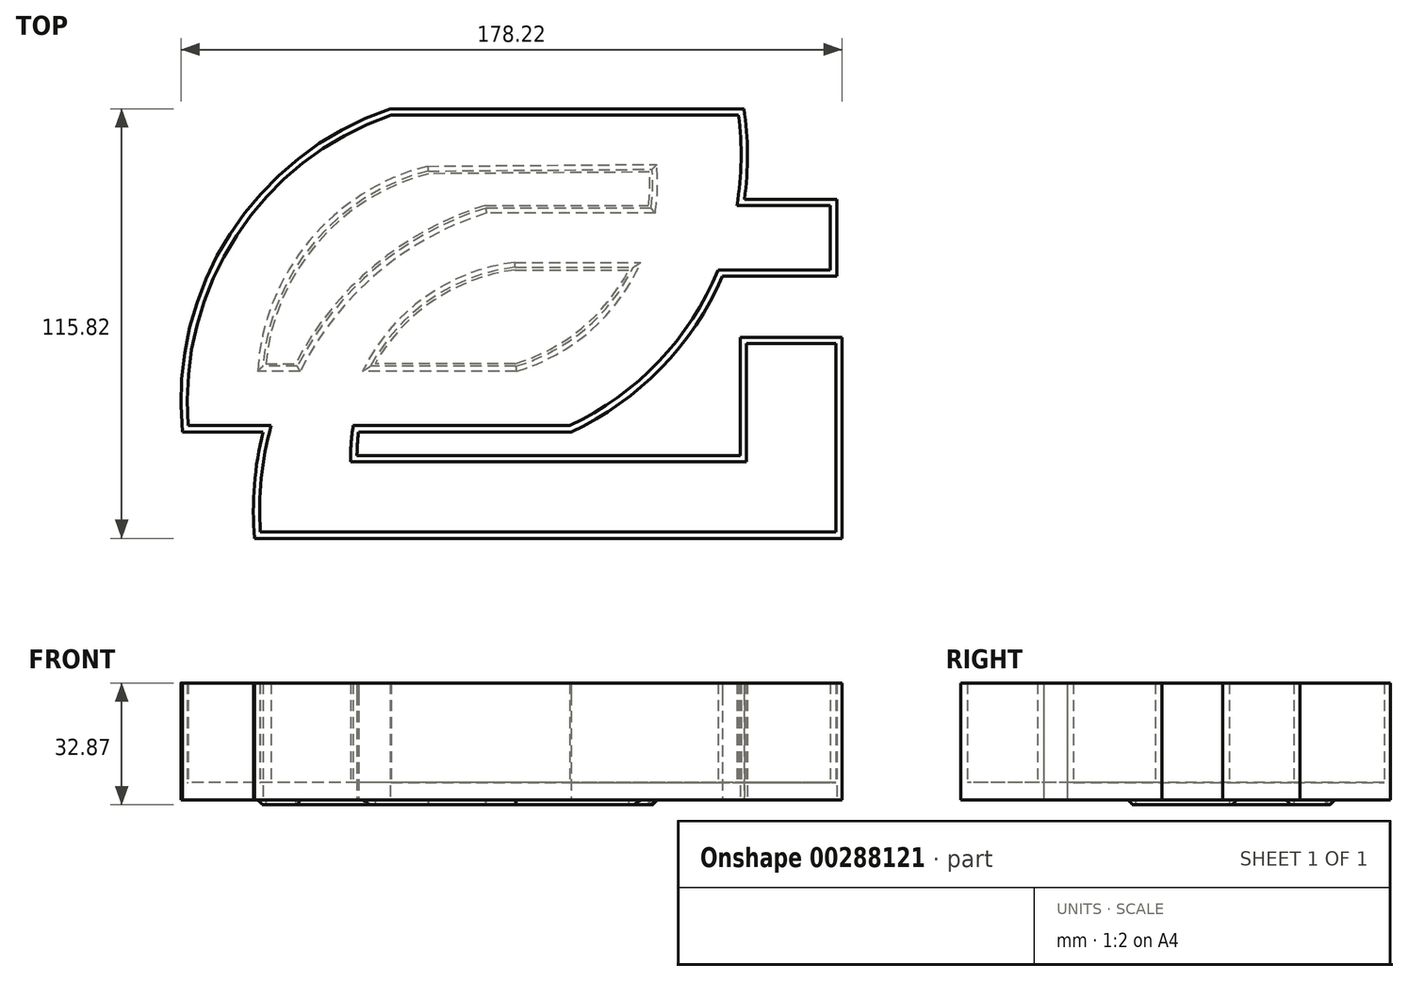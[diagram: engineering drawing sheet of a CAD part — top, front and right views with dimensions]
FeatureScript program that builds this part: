
annotation { "Feature Type Name" : "Feature", "Feature Type Description" : "" }
export const myFeature = defineFeature(function(context is Context, id is Id, definition is map)
    precondition{}
    {
        {
            assignVariable(context, id + "F0", {"name" : "wt", "anyValue" : 1.7});
        }
        {
            assignVariable(context, id + "F1", {"name" : "wd", "anyValue" : 28.57 * mm});
        }
        {
            var Q0;
            Q0=qCreatedBy(makeId("Top.planeOp"),FACE);
            var sketch = newSketch(context, id + "F2", { "sketchPlane" : qUnion([Q0])});
            skLineSegment(sketch, "E0", {"start": v(61.61, -3.74) * mm, "end": v(89.1, -3.74) * mm});
            skLineSegment(sketch, "E1", {"start": v(89.1, -3.74) * mm, "end": v(89.1, -57.9) * mm});
            skLineSegment(sketch, "E2", {"start": v(89.1, -57.9) * mm, "end": v(-69.28, -57.9) * mm});
            skLineSegment(sketch, "E3", {"start": v(61.61, -3.74) * mm, "end": v(61.61, -35.58) * mm});
            skLineSegment(sketch, "E4", {"start": v(61.61, -35.58) * mm, "end": v(-41.66, -35.58) * mm});
            skArc(sketch, "E5", {"start": v(1.12, 12.73) * mm, "mid": v(-29.38, -3.36) * mm, "end": v(-41.66, -35.58) * mm});
            skLineSegment(sketch, "E6", {"start": v(1.12, 12.73) * mm, "end": v(28.71, 12.73) * mm});
            skLineSegment(sketch, "E7", {"start": v(56.87, 12.73) * mm, "end": v(87.68, 12.73) * mm});
            skLineSegment(sketch, "E8", {"start": v(87.68, 12.73) * mm, "end": v(87.68, 33.53) * mm});
            skLineSegment(sketch, "E9", {"start": v(87.68, 33.53) * mm, "end": v(61.61, 33.53) * mm});
            skLineSegment(sketch, "E10", {"start": v(35.42, 33.53) * mm, "end": v(-7.33, 33.53) * mm});
            skArc(sketch, "E11", {"start": v(-7.33, 33.53) * mm, "mid": v(-54.5, -1.23) * mm, "end": v(-69.28, -57.9) * mm});
            skArc(sketch, "E12", {"start": v(-32.72, 57.9) * mm, "mid": v(-75.9, 24.1) * mm, "end": v(-88.7, -29.22) * mm});
            skLineSegment(sketch, "E13", {"start": v(-32.72, 57.9) * mm, "end": v(62.63, 57.9) * mm});
            skArc(sketch, "E14", {"start": v(16.1, -29.22) * mm, "mid": v(53.9, 6.58) * mm, "end": v(62.63, 57.9) * mm});
            skLineSegment(sketch, "E15", {"start": v(16.1, -29.22) * mm, "end": v(-41.22, -29.22) * mm});
            skLineSegment(sketch, "E16", {"start": v(-67, -29.22) * mm, "end": v(-88.7, -29.22) * mm});
            skArc(sketch, "E17", {"start": v(-22.14, 38.67) * mm, "mid": v(-50.54, 21.24) * mm, "end": v(-64.34, -9.1) * mm});
            skLineSegment(sketch, "E18", {"start": v(-22.14, 38.67) * mm, "end": v(35.58, 39.1) * mm});
            skArc(sketch, "E19", {"start": v(0.76, -9.1) * mm, "mid": v(26.34, 9.11) * mm, "end": v(35.58, 39.1) * mm});
            skLineSegment(sketch, "E20", {"start": v(0.76, -9.1) * mm, "end": v(-33.75, -9.1) * mm});
            skLineSegment(sketch, "E21", {"start": v(-59.24, -9.1) * mm, "end": v(-64.34, -9.1) * mm});
            skSolve(sketch);
        }
        {
            var Q0;
            Q0=makeQuery(id+"F2.imprint","IMPRINT",FACE,{"disambiguationData":[TD([[makeQuery(id+"F2.imprint","IMPRINT",EDGE,{"derivedFrom":sQuery(id+"F2.wireOp",EDGE,"E12")}),1.0]])]});
            extrude(context, id + "F3", {"entities" : qUnion([Q0]), "depth" : getVariable(context, 'wd')});
        }
        {
            var Q0;
            Q0=makeQuery(id+"F2.imprint","IMPRINT",FACE,{"disambiguationData":[TD([[makeQuery(id+"F2.imprint","IMPRINT",EDGE,{"derivedFrom":sQuery(id+"F2.wireOp",EDGE,"E0")}),-1.0]])]});
            extrude(context, id + "F4", {"entities" : qUnion([Q0]), "operationType" : NewBodyOperationType.ADD, "depth" : getVariable(context, 'wd')});
        }
        {
            var Q0;
            {var subQ0=sQuery(id+"F2.wireOp",EDGE,"E7");Q0=makeQuery(id+"F2.imprint","IMPRINT",FACE,{"disambiguationData":[TD([[makeQuery(id+"F2.imprint","IMPRINT",EDGE,{"derivedFrom":subQ0}),1.0]])]});}
            extrude(context, id + "F5", {"entities" : qUnion([Q0]), "operationType" : NewBodyOperationType.ADD, "depth" : getVariable(context, 'wd')});
        }
        {
            var Q0;
            Q0=makeQuery(id+"F3.opExtrude","CAP_FACE",FACE,{"disambiguationData":[OSD([sQuery(id+"F2.wireOp",EDGE,"E5"),sQuery(id+"F2.wireOp",EDGE,"E11"),sQuery(id+"F2.wireOp",EDGE,"E12"),sQuery(id+"F2.wireOp",EDGE,"E13"),sQuery(id+"F2.wireOp",EDGE,"E14"),sQuery(id+"F2.wireOp",EDGE,"E15"),sQuery(id+"F2.wireOp",EDGE,"E16"),sQuery(id+"F2.wireOp",EDGE,"E17"),sQuery(id+"F2.wireOp",EDGE,"E18"),sQuery(id+"F2.wireOp",EDGE,"E19"),sQuery(id+"F2.wireOp",EDGE,"E20"),sQuery(id+"F2.wireOp",EDGE,"E21")])],"isStart":false});
            var Q1;
            Q1=makeQuery(id+"F4.opExtrude","CAP_FACE",FACE,{"disambiguationData":[OSD([sQuery(id+"F2.wireOp",EDGE,"E0"),sQuery(id+"F2.wireOp",EDGE,"E1"),sQuery(id+"F2.wireOp",EDGE,"E2"),sQuery(id+"F2.wireOp",EDGE,"E3"),sQuery(id+"F2.wireOp",EDGE,"E4"),sQuery(id+"F2.wireOp",EDGE,"E5"),sQuery(id+"F2.wireOp",EDGE,"E6"),sQuery(id+"F2.wireOp",EDGE,"E10"),sQuery(id+"F2.wireOp",EDGE,"E11"),sQuery(id+"F2.wireOp",EDGE,"E19")])],"isStart":false});
            var Q2;
            Q2=makeQuery(id+"F5.opExtrude","CAP_FACE",FACE,{"disambiguationData":[OSD([sQuery(id+"F2.wireOp",EDGE,"E7"),sQuery(id+"F2.wireOp",EDGE,"E8"),sQuery(id+"F2.wireOp",EDGE,"E9"),sQuery(id+"F2.wireOp",EDGE,"E14")])],"isStart":false});
            shell(context, id + "F6", {"entities" : qUnion([Q0, Q1, Q2]), "thickness" : (getVariable(context, 'wt')) * mm});
        }
        {
            var Q0;
            {var subQ0=sQuery(id+"F2.wireOp",EDGE,"E14");var subQ1=sQuery(id+"F2.wireOp",EDGE,"E9");var subQ2=sQuery(id+"F2.wireOp",EDGE,"E8");var subQ3=sQuery(id+"F2.wireOp",EDGE,"E7");var subQ4=sQuery(id+"F2.wireOp",EDGE,"E19");var subQ5=sQuery(id+"F2.wireOp",EDGE,"E11");var subQ6=sQuery(id+"F2.wireOp",EDGE,"E10");var subQ7=sQuery(id+"F2.wireOp",EDGE,"E6");var subQ8=sQuery(id+"F2.wireOp",EDGE,"E5");var subQ9=sQuery(id+"F2.wireOp",EDGE,"E4");var subQ10=sQuery(id+"F2.wireOp",EDGE,"E3");var subQ11=sQuery(id+"F2.wireOp",EDGE,"E2");var subQ12=sQuery(id+"F2.wireOp",EDGE,"E1");var subQ13=sQuery(id+"F2.wireOp",EDGE,"E0");var subQ14=sQuery(id+"F2.wireOp",EDGE,"E21");var subQ15=sQuery(id+"F2.wireOp",EDGE,"E20");var subQ16=sQuery(id+"F2.wireOp",EDGE,"E18");var subQ17=sQuery(id+"F2.wireOp",EDGE,"E17");var subQ18=sQuery(id+"F2.wireOp",EDGE,"E16");var subQ19=sQuery(id+"F2.wireOp",EDGE,"E15");var subQ20=sQuery(id+"F2.wireOp",EDGE,"E13");var subQ21=sQuery(id+"F2.wireOp",EDGE,"E12");Q0=makeQuery(id+"F6.opShell","OFFSET_FACE",FACE,{"disambiguationData":[OSD([subQ13,subQ12,subQ11,subQ10,subQ9,subQ8,subQ7,subQ3,subQ2,subQ1,subQ6,subQ5,subQ21,subQ20,subQ0,subQ19,subQ18,subQ17,subQ16,subQ4,subQ15,subQ14]),TDD([makeQuery(id+"F5.boolean.opBoolean","MERGE",FACE,{"derivedFrom":[makeQuery(id+"F4.boolean.opBoolean","MERGE",FACE,{"derivedFrom":[makeQuery(id+"F3.opExtrude","CAP_FACE",FACE,{"disambiguationData":[OSD([subQ8,subQ5,subQ21,subQ20,subQ0,subQ19,subQ18,subQ17,subQ16,subQ4,subQ15,subQ14])],"isStart":false}),makeQuery(id+"F4.opExtrude","CAP_FACE",FACE,{"disambiguationData":[OSD([subQ13,subQ12,subQ11,subQ10,subQ9,subQ8,subQ7,subQ6,subQ5,subQ4])],"isStart":false})]}),makeQuery(id+"F5.opExtrude","CAP_FACE",FACE,{"disambiguationData":[OSD([subQ3,subQ2,subQ1,subQ0])],"isStart":false})]})]),OD(0.0)]});}
            cPlane(context, id + "F7", {"entities" : qUnion([Q0]), "cplaneType" : CPlaneType.OFFSET, "offset" : 3 * mm, "oppositeDirection" : true, "width" : 150 * mm, "height" : 150 * mm});
        }
        {
            var Q0;
            Q0=qCreatedBy(id+"F7.planeOp",FACE);
            var sketch = newSketch(context, id + "F8", { "sketchPlane" : qUnion([Q0])});
            skArc(sketch, "E22.0.0", {"start": v(-41.66, -35.58) * mm, "mid": v(-41.54, -32.4) * mm, "end": v(-41.22, -29.22) * mm});
            skLineSegment(sketch, "E22.0.1", {"start": v(-41.22, -29.22) * mm, "end": v(16.1, -29.22) * mm});
            skArc(sketch, "E22.0.2", {"start": v(16.1, -29.22) * mm, "mid": v(40.34, -12) * mm, "end": v(56.87, 12.73) * mm});
            skLineSegment(sketch, "E22.0.3", {"start": v(56.87, 12.73) * mm, "end": v(87.68, 12.73) * mm});
            skLineSegment(sketch, "E22.0.4", {"start": v(87.68, 12.73) * mm, "end": v(87.68, 33.53) * mm});
            skLineSegment(sketch, "E22.0.5", {"start": v(87.68, 33.53) * mm, "end": v(62.75, 33.53) * mm});
            skArc(sketch, "E22.0.6", {"start": v(62.75, 33.53) * mm, "mid": v(63.6, 45.72) * mm, "end": v(62.63, 57.9) * mm});
            skLineSegment(sketch, "E22.0.7", {"start": v(62.63, 57.9) * mm, "end": v(-32.72, 57.9) * mm});
            skArc(sketch, "E22.0.8", {"start": v(-32.72, 57.9) * mm, "mid": v(-75.9, 24.1) * mm, "end": v(-88.7, -29.22) * mm});
            skLineSegment(sketch, "E22.0.9", {"start": v(-88.7, -29.22) * mm, "end": v(-67, -29.22) * mm});
            skArc(sketch, "E22.0.10", {"start": v(-67, -29.22) * mm, "mid": v(-69.32, -43.47) * mm, "end": v(-69.28, -57.9) * mm});
            skLineSegment(sketch, "E22.0.11", {"start": v(-69.28, -57.9) * mm, "end": v(89.1, -57.9) * mm});
            skLineSegment(sketch, "E22.0.12", {"start": v(89.1, -57.9) * mm, "end": v(89.1, -3.74) * mm});
            skLineSegment(sketch, "E22.0.13", {"start": v(89.1, -3.74) * mm, "end": v(61.61, -3.74) * mm});
            skLineSegment(sketch, "E22.0.14", {"start": v(61.61, -3.74) * mm, "end": v(61.61, -35.58) * mm});
            skLineSegment(sketch, "E22.0.15", {"start": v(61.61, -35.58) * mm, "end": v(-41.66, -35.58) * mm});
            skLineSegment(sketch, "E23.0.0", {"start": v(-36.77, -10.8) * mm, "end": v(1.01, -10.8) * mm});
            skArc(sketch, "E23.0.1", {"start": v(1.01, -10.8) * mm, "mid": v(18.88, -1.3) * mm, "end": v(31.6, 14.43) * mm});
            skLineSegment(sketch, "E23.0.2", {"start": v(31.6, 14.43) * mm, "end": v(1.01, 14.43) * mm});
            skArc(sketch, "E23.0.3", {"start": v(1.01, 14.43) * mm, "mid": v(-20.87, 6.3) * mm, "end": v(-36.77, -10.8) * mm});
            skLineSegment(sketch, "E24.0.0", {"start": v(-7.08, 31.83) * mm, "end": v(36.95, 31.83) * mm});
            skArc(sketch, "E24.0.1", {"start": v(36.95, 31.83) * mm, "mid": v(37.28, 36.32) * mm, "end": v(37.2, 40.82) * mm});
            skLineSegment(sketch, "E24.0.2", {"start": v(37.2, 40.82) * mm, "end": v(-22.37, 40.37) * mm});
            skArc(sketch, "E24.0.3", {"start": v(-22.37, 40.37) * mm, "mid": v(-52.38, 21.71) * mm, "end": v(-66.24, -10.8) * mm});
            skLineSegment(sketch, "E24.0.4", {"start": v(-66.24, -10.8) * mm, "end": v(-58.22, -10.8) * mm});
            skArc(sketch, "E24.0.5", {"start": v(-58.22, -10.8) * mm, "mid": v(-36.94, 15.66) * mm, "end": v(-7.08, 31.83) * mm});
            skArc(sketch, "E25.0", {"start": v(-32.43, 56.2) * mm, "mid": v(-74.13, 23.72) * mm, "end": v(-87.14, -27.52) * mm});
            skLineSegment(sketch, "E26.0.0", {"start": v(-64.79, -27.52) * mm, "end": v(-87.14, -27.52) * mm});
            skLineSegment(sketch, "E26.0.2", {"start": v(-87.14, -27.52) * mm, "end": v(-64.79, -27.52) * mm});
            skArc(sketch, "E27.0.0", {"start": v(-64.79, -27.52) * mm, "mid": v(-67.46, -41.74) * mm, "end": v(-67.7, -56.2) * mm});
            skArc(sketch, "E27.0.2", {"start": v(-67.7, -56.2) * mm, "mid": v(-67.46, -41.74) * mm, "end": v(-64.79, -27.52) * mm});
            skLineSegment(sketch, "E28.0.0", {"start": v(-32.43, 56.2) * mm, "end": v(61.16, 56.2) * mm});
            skLineSegment(sketch, "E28.0.2", {"start": v(61.16, 56.2) * mm, "end": v(-32.43, 56.2) * mm});
            skLineSegment(sketch, "E29.0.0", {"start": v(87.4, -56.2) * mm, "end": v(-67.7, -56.2) * mm});
            skLineSegment(sketch, "E29.0.2", {"start": v(-67.7, -56.2) * mm, "end": v(87.4, -56.2) * mm});
            skLineSegment(sketch, "E30.0.0", {"start": v(-43.34, -37.28) * mm, "end": v(63.31, -37.28) * mm});
            skLineSegment(sketch, "E30.0.2", {"start": v(63.31, -37.28) * mm, "end": v(-43.34, -37.28) * mm});
            skLineSegment(sketch, "E31.0.0", {"start": v(63.31, -5.44) * mm, "end": v(87.4, -5.44) * mm});
            skLineSegment(sketch, "E31.0.2", {"start": v(87.4, -5.44) * mm, "end": v(63.31, -5.44) * mm});
            skLineSegment(sketch, "E32.0.0", {"start": v(87.4, -5.44) * mm, "end": v(87.4, -56.2) * mm});
            skLineSegment(sketch, "E32.0.2", {"start": v(87.4, -56.2) * mm, "end": v(87.4, -5.44) * mm});
            skLineSegment(sketch, "E33.0.0", {"start": v(63.31, -37.28) * mm, "end": v(63.31, -5.44) * mm});
            skLineSegment(sketch, "E33.0.2", {"start": v(63.31, -5.44) * mm, "end": v(63.31, -37.28) * mm});
            skArc(sketch, "E34.0.1", {"start": v(-42.69, -27.52) * mm, "mid": v(-43.25, -32.39) * mm, "end": v(-43.34, -37.28) * mm});
            skArc(sketch, "E34.0.3", {"start": v(-43.34, -37.28) * mm, "mid": v(-43.25, -32.39) * mm, "end": v(-42.69, -27.52) * mm});
            skLineSegment(sketch, "E35.0.0", {"start": v(15.72, -27.52) * mm, "end": v(-42.69, -27.52) * mm});
            skLineSegment(sketch, "E35.0.2", {"start": v(-42.69, -27.52) * mm, "end": v(15.72, -27.52) * mm});
            skArc(sketch, "E36.0.1", {"start": v(55.74, 14.43) * mm, "mid": v(39.64, -10.27) * mm, "end": v(15.72, -27.52) * mm});
            skArc(sketch, "E36.0.3", {"start": v(15.72, -27.52) * mm, "mid": v(39.64, -10.27) * mm, "end": v(55.74, 14.43) * mm});
            skLineSegment(sketch, "E37.0.0", {"start": v(85.98, 14.43) * mm, "end": v(55.74, 14.43) * mm});
            skLineSegment(sketch, "E37.0.2", {"start": v(55.74, 14.43) * mm, "end": v(85.98, 14.43) * mm});
            skLineSegment(sketch, "E38.0.0", {"start": v(85.98, 31.83) * mm, "end": v(85.98, 14.43) * mm});
            skLineSegment(sketch, "E38.0.2", {"start": v(85.98, 14.43) * mm, "end": v(85.98, 31.83) * mm});
            skArc(sketch, "E39.0.0", {"start": v(60.76, 31.83) * mm, "mid": v(61.89, 44) * mm, "end": v(61.16, 56.2) * mm});
            skArc(sketch, "E39.0.2", {"start": v(61.16, 56.2) * mm, "mid": v(61.89, 44) * mm, "end": v(60.76, 31.83) * mm});
            skLineSegment(sketch, "E40.0.0", {"start": v(60.76, 31.83) * mm, "end": v(85.98, 31.83) * mm});
            skLineSegment(sketch, "E40.0.2", {"start": v(85.98, 31.83) * mm, "end": v(60.76, 31.83) * mm});
            skArc(sketch, "E41.0.0", {"start": v(-87.14, -27.52) * mm, "mid": v(-74.13, 23.72) * mm, "end": v(-32.43, 56.2) * mm});
            skArc(sketch, "E42.0", {"start": v(-63.88, -52.2) * mm, "mid": v(-62.9, -37.67) * mm, "end": v(-59.36, -23.52) * mm});
            skLineSegment(sketch, "E42.1", {"start": v(-83.36, -23.52) * mm, "end": v(-59.36, -23.52) * mm});
            skArc(sketch, "E42.2", {"start": v(-31.76, 52.2) * mm, "mid": v(-69.95, 22.78) * mm, "end": v(-83.36, -23.52) * mm});
            skLineSegment(sketch, "E42.3", {"start": v(-31.76, 52.2) * mm, "end": v(57.59, 52.2) * mm});
            skArc(sketch, "E42.4", {"start": v(57.59, 52.2) * mm, "mid": v(57.71, 39.95) * mm, "end": v(55.87, 27.83) * mm});
            skLineSegment(sketch, "E42.5", {"start": v(67.31, -41.28) * mm, "end": v(-47.08, -41.28) * mm});
            skLineSegment(sketch, "E42.6", {"start": v(67.31, -9.44) * mm, "end": v(67.31, -41.28) * mm});
            skLineSegment(sketch, "E42.7", {"start": v(83.4, -9.44) * mm, "end": v(67.31, -9.44) * mm});
            skLineSegment(sketch, "E42.8", {"start": v(83.4, -52.2) * mm, "end": v(83.4, -9.44) * mm});
            skArc(sketch, "E42.9", {"start": v(-47.08, -41.28) * mm, "mid": v(-47.25, -32.36) * mm, "end": v(-45.97, -23.52) * mm});
            skLineSegment(sketch, "E42.10", {"start": v(-45.97, -23.52) * mm, "end": v(14.8, -23.52) * mm});
            skArc(sketch, "E42.11", {"start": v(53.02, 18.43) * mm, "mid": v(37.95, -6.22) * mm, "end": v(14.8, -23.52) * mm});
            skLineSegment(sketch, "E42.12", {"start": v(53.02, 18.43) * mm, "end": v(81.98, 18.43) * mm});
            skLineSegment(sketch, "E42.13", {"start": v(81.98, 18.43) * mm, "end": v(81.98, 27.83) * mm});
            skLineSegment(sketch, "E42.14", {"start": v(-63.88, -52.2) * mm, "end": v(83.4, -52.2) * mm});
            skLineSegment(sketch, "E42.15", {"start": v(81.98, 27.83) * mm, "end": v(55.87, 27.83) * mm});
            skLineSegment(sketch, "E43.0", {"start": v(37.77, 18.43) * mm, "end": v(0.77, 18.43) * mm});
            skArc(sketch, "E43.1", {"start": v(1.58, -14.8) * mm, "mid": v(23.62, -2.48) * mm, "end": v(37.77, 18.43) * mm});
            skLineSegment(sketch, "E43.2", {"start": v(-43.18, -14.8) * mm, "end": v(1.58, -14.8) * mm});
            skArc(sketch, "E43.3", {"start": v(0.77, 18.43) * mm, "mid": v(-25.7, 7.77) * mm, "end": v(-43.18, -14.8) * mm});
            skArc(sketch, "E44.0", {"start": v(-55.75, -14.8) * mm, "mid": v(-35.52, 11.62) * mm, "end": v(-6.47, 27.83) * mm});
            skArc(sketch, "E44.1", {"start": v(40.39, 27.83) * mm, "mid": v(41.28, 36.32) * mm, "end": v(40.84, 44.85) * mm});
            skLineSegment(sketch, "E44.2", {"start": v(40.84, 44.85) * mm, "end": v(-22.88, 44.37) * mm});
            skLineSegment(sketch, "E44.3", {"start": v(-6.47, 27.83) * mm, "end": v(40.39, 27.83) * mm});
            skArc(sketch, "E44.4", {"start": v(-22.88, 44.37) * mm, "mid": v(-56.66, 22.81) * mm, "end": v(-70.5, -14.8) * mm});
            skLineSegment(sketch, "E44.5", {"start": v(-70.5, -14.8) * mm, "end": v(-55.75, -14.8) * mm});
            skSolve(sketch);
        }
        {
            var Q0;
            Q0=makeQuery(id+"F8.imprint","IMPRINT",FACE,{"disambiguationData":[TD([[makeQuery(id+"F8.imprint","IMPRINT",EDGE,{"derivedFrom":sQuery(id+"F8.wireOp",EDGE,"E26.0.2")}),1.0]])]});
            var Q1;
            Q1=makeQuery(id+"F8.imprint","IMPRINT",FACE,{"disambiguationData":[TD([[makeQuery(id+"F8.imprint","IMPRINT",EDGE,{"derivedFrom":sQuery(id+"F8.wireOp",EDGE,"E24.0.0")}),-1.0]])]});
            var Q2;
            Q2=makeQuery(id+"F8.imprint","IMPRINT",FACE,{"disambiguationData":[TD([[makeQuery(id+"F8.imprint","IMPRINT",EDGE,{"derivedFrom":sQuery(id+"F8.wireOp",EDGE,"E23.0.0")}),-1.0]])]});
            extrude(context, id + "F9", {"entities" : qUnion([Q0, Q1, Q2]), "depth" : 3 * mm});
        }
        {
            var Q0;
            Q0=makeQuery(id+"F9.opExtrude","CAP_EDGE",EDGE,{"disambiguationData":[OSD([sQuery(id+"F8.wireOp",EDGE,"E44.2")])],"isStart":true});
            var Q1;
            Q1=makeQuery(id+"F9.opExtrude","CAP_EDGE",EDGE,{"disambiguationData":[OSD([sQuery(id+"F8.wireOp",EDGE,"E44.1")])],"isStart":true});
            var Q2;
            Q2=makeQuery(id+"F9.opExtrude","CAP_EDGE",EDGE,{"disambiguationData":[OSD([sQuery(id+"F8.wireOp",EDGE,"E44.3")])],"isStart":true});
            var Q3;
            Q3=makeQuery(id+"F9.opExtrude","CAP_EDGE",EDGE,{"disambiguationData":[OSD([sQuery(id+"F8.wireOp",EDGE,"E44.0")])],"isStart":true});
            var Q4;
            Q4=makeQuery(id+"F9.opExtrude","CAP_EDGE",EDGE,{"disambiguationData":[OSD([sQuery(id+"F8.wireOp",EDGE,"E44.4")])],"isStart":true});
            var Q5;
            Q5=makeQuery(id+"F9.opExtrude","CAP_EDGE",EDGE,{"disambiguationData":[OSD([sQuery(id+"F8.wireOp",EDGE,"E42.2")])],"isStart":true});
            var Q6;
            Q6=makeQuery(id+"F9.opExtrude","CAP_EDGE",EDGE,{"disambiguationData":[OSD([sQuery(id+"F8.wireOp",EDGE,"E42.3")])],"isStart":true});
            var Q7;
            Q7=makeQuery(id+"F9.opExtrude","CAP_EDGE",EDGE,{"disambiguationData":[OSD([sQuery(id+"F8.wireOp",EDGE,"E42.1")])],"isStart":true});
            var Q8;
            Q8=makeQuery(id+"F9.opExtrude","CAP_EDGE",EDGE,{"disambiguationData":[OSD([sQuery(id+"F8.wireOp",EDGE,"E42.0")])],"isStart":true});
            var Q9;
            Q9=makeQuery(id+"F9.opExtrude","CAP_EDGE",EDGE,{"disambiguationData":[OSD([sQuery(id+"F8.wireOp",EDGE,"E42.14")])],"isStart":true});
            var Q10;
            Q10=makeQuery(id+"F9.opExtrude","CAP_EDGE",EDGE,{"disambiguationData":[OSD([sQuery(id+"F8.wireOp",EDGE,"E42.5")])],"isStart":true});
            var Q11;
            Q11=makeQuery(id+"F9.opExtrude","CAP_EDGE",EDGE,{"disambiguationData":[OSD([sQuery(id+"F8.wireOp",EDGE,"E42.9")])],"isStart":true});
            var Q12;
            Q12=makeQuery(id+"F9.opExtrude","CAP_EDGE",EDGE,{"disambiguationData":[OSD([sQuery(id+"F8.wireOp",EDGE,"E42.10")])],"isStart":true});
            var Q13;
            Q13=makeQuery(id+"F9.opExtrude","CAP_EDGE",EDGE,{"disambiguationData":[OSD([sQuery(id+"F8.wireOp",EDGE,"E42.6")])],"isStart":true});
            var Q14;
            Q14=makeQuery(id+"F9.opExtrude","CAP_EDGE",EDGE,{"disambiguationData":[OSD([sQuery(id+"F8.wireOp",EDGE,"E42.7")])],"isStart":true});
            var Q15;
            Q15=makeQuery(id+"F9.opExtrude","CAP_EDGE",EDGE,{"disambiguationData":[OSD([sQuery(id+"F8.wireOp",EDGE,"E42.8")])],"isStart":true});
            var Q16;
            Q16=makeQuery(id+"F9.opExtrude","CAP_EDGE",EDGE,{"disambiguationData":[OSD([sQuery(id+"F8.wireOp",EDGE,"E42.11")])],"isStart":true});
            var Q17;
            Q17=makeQuery(id+"F9.opExtrude","CAP_EDGE",EDGE,{"disambiguationData":[OSD([sQuery(id+"F8.wireOp",EDGE,"E42.12")])],"isStart":true});
            var Q18;
            Q18=makeQuery(id+"F9.opExtrude","CAP_EDGE",EDGE,{"disambiguationData":[OSD([sQuery(id+"F8.wireOp",EDGE,"E42.15")])],"isStart":true});
            var Q19;
            Q19=makeQuery(id+"F9.opExtrude","CAP_EDGE",EDGE,{"disambiguationData":[OSD([sQuery(id+"F8.wireOp",EDGE,"E42.13")])],"isStart":true});
            var Q20;
            Q20=makeQuery(id+"F9.opExtrude","CAP_EDGE",EDGE,{"disambiguationData":[OSD([sQuery(id+"F8.wireOp",EDGE,"E42.4")])],"isStart":true});
            var Q21;
            Q21=makeQuery(id+"F9.opExtrude","CAP_EDGE",EDGE,{"disambiguationData":[OSD([sQuery(id+"F8.wireOp",EDGE,"E44.5")])],"isStart":true});
            var Q22;
            Q22=makeQuery(id+"F9.opExtrude","CAP_EDGE",EDGE,{"disambiguationData":[OSD([sQuery(id+"F8.wireOp",EDGE,"E43.2")])],"isStart":true});
            var Q23;
            Q23=makeQuery(id+"F9.opExtrude","CAP_EDGE",EDGE,{"disambiguationData":[OSD([sQuery(id+"F8.wireOp",EDGE,"E43.1")])],"isStart":true});
            var Q24;
            Q24=makeQuery(id+"F9.opExtrude","CAP_EDGE",EDGE,{"disambiguationData":[OSD([sQuery(id+"F8.wireOp",EDGE,"E43.0")])],"isStart":true});
            var Q25;
            Q25=makeQuery(id+"F9.opExtrude","CAP_EDGE",EDGE,{"disambiguationData":[OSD([sQuery(id+"F8.wireOp",EDGE,"E43.3")])],"isStart":true});
            chamfer(context, id + "F10", {"entities" : qUnion([Q0, Q1, Q2, Q3, Q4, Q5, Q6, Q7, Q8, Q9, Q10, Q11, Q12, Q13, Q14, Q15, Q16, Q17, Q18, Q19, Q20, Q21, Q22, Q23, Q24, Q25]), "width" : 3.25 * mm, "tangentPropagation" : true});
        }
        {
            var Q0;
            {var subQ0=sQuery(id+"F2.wireOp",EDGE,"E14");var subQ1=sQuery(id+"F2.wireOp",EDGE,"E9");var subQ2=sQuery(id+"F2.wireOp",EDGE,"E8");var subQ3=sQuery(id+"F2.wireOp",EDGE,"E7");var subQ4=sQuery(id+"F2.wireOp",EDGE,"E19");var subQ5=sQuery(id+"F2.wireOp",EDGE,"E11");var subQ6=sQuery(id+"F2.wireOp",EDGE,"E10");var subQ7=sQuery(id+"F2.wireOp",EDGE,"E6");var subQ8=sQuery(id+"F2.wireOp",EDGE,"E5");var subQ9=sQuery(id+"F2.wireOp",EDGE,"E4");var subQ10=sQuery(id+"F2.wireOp",EDGE,"E3");var subQ11=sQuery(id+"F2.wireOp",EDGE,"E2");var subQ12=sQuery(id+"F2.wireOp",EDGE,"E1");var subQ13=sQuery(id+"F2.wireOp",EDGE,"E0");var subQ14=sQuery(id+"F2.wireOp",EDGE,"E21");var subQ15=sQuery(id+"F2.wireOp",EDGE,"E20");var subQ16=sQuery(id+"F2.wireOp",EDGE,"E18");var subQ17=sQuery(id+"F2.wireOp",EDGE,"E17");var subQ18=sQuery(id+"F2.wireOp",EDGE,"E16");var subQ19=sQuery(id+"F2.wireOp",EDGE,"E15");var subQ20=sQuery(id+"F2.wireOp",EDGE,"E13");var subQ21=sQuery(id+"F2.wireOp",EDGE,"E12");Q0=makeQuery(id+"F6.opShell","OFFSET_FACE",FACE,{"disambiguationData":[OSD([subQ13,subQ12,subQ11,subQ10,subQ9,subQ8,subQ7,subQ3,subQ2,subQ1,subQ6,subQ5,subQ21,subQ20,subQ0,subQ19,subQ18,subQ17,subQ16,subQ4,subQ15,subQ14]),TDD([makeQuery(id+"F5.boolean.opBoolean","MERGE",FACE,{"derivedFrom":[makeQuery(id+"F4.boolean.opBoolean","MERGE",FACE,{"derivedFrom":[makeQuery(id+"F3.opExtrude","CAP_FACE",FACE,{"disambiguationData":[OSD([subQ8,subQ5,subQ21,subQ20,subQ0,subQ19,subQ18,subQ17,subQ16,subQ4,subQ15,subQ14])],"isStart":false}),makeQuery(id+"F4.opExtrude","CAP_FACE",FACE,{"disambiguationData":[OSD([subQ13,subQ12,subQ11,subQ10,subQ9,subQ8,subQ7,subQ6,subQ5,subQ4])],"isStart":false})]}),makeQuery(id+"F5.opExtrude","CAP_FACE",FACE,{"disambiguationData":[OSD([subQ3,subQ2,subQ1,subQ0])],"isStart":false})]})]),OD(0.0)]});}
            var Q1;
            {var subQ0=sQuery(id+"F2.wireOp",EDGE,"E14");var subQ1=sQuery(id+"F2.wireOp",EDGE,"E19");var subQ2=sQuery(id+"F2.wireOp",EDGE,"E11");var subQ3=sQuery(id+"F2.wireOp",EDGE,"E5");Q1=makeQuery(id+"F5.boolean.opBoolean","MERGE",FACE,{"derivedFrom":[makeQuery(id+"F4.boolean.opBoolean","MERGE",FACE,{"derivedFrom":[makeQuery(id+"F3.opExtrude","CAP_FACE",FACE,{"disambiguationData":[OSD([subQ3,subQ2,sQuery(id+"F2.wireOp",EDGE,"E12"),sQuery(id+"F2.wireOp",EDGE,"E13"),subQ0,sQuery(id+"F2.wireOp",EDGE,"E15"),sQuery(id+"F2.wireOp",EDGE,"E16"),sQuery(id+"F2.wireOp",EDGE,"E17"),sQuery(id+"F2.wireOp",EDGE,"E18"),subQ1,sQuery(id+"F2.wireOp",EDGE,"E20"),sQuery(id+"F2.wireOp",EDGE,"E21")])],"isStart":false}),makeQuery(id+"F4.opExtrude","CAP_FACE",FACE,{"disambiguationData":[OSD([sQuery(id+"F2.wireOp",EDGE,"E0"),sQuery(id+"F2.wireOp",EDGE,"E1"),sQuery(id+"F2.wireOp",EDGE,"E2"),sQuery(id+"F2.wireOp",EDGE,"E3"),sQuery(id+"F2.wireOp",EDGE,"E4"),subQ3,sQuery(id+"F2.wireOp",EDGE,"E6"),sQuery(id+"F2.wireOp",EDGE,"E10"),subQ2,subQ1])],"isStart":false})]}),makeQuery(id+"F5.opExtrude","CAP_FACE",FACE,{"disambiguationData":[OSD([sQuery(id+"F2.wireOp",EDGE,"E7"),sQuery(id+"F2.wireOp",EDGE,"E8"),sQuery(id+"F2.wireOp",EDGE,"E9"),subQ0])],"isStart":false})]});}
            var Q2;
            {var subQ0=sQuery(id+"F2.wireOp",EDGE,"E14");var subQ1=sQuery(id+"F2.wireOp",EDGE,"E9");var subQ2=sQuery(id+"F2.wireOp",EDGE,"E8");var subQ3=sQuery(id+"F2.wireOp",EDGE,"E7");var subQ4=sQuery(id+"F2.wireOp",EDGE,"E19");var subQ5=sQuery(id+"F2.wireOp",EDGE,"E11");var subQ6=sQuery(id+"F2.wireOp",EDGE,"E10");var subQ7=sQuery(id+"F2.wireOp",EDGE,"E6");var subQ8=sQuery(id+"F2.wireOp",EDGE,"E5");var subQ9=sQuery(id+"F2.wireOp",EDGE,"E4");var subQ10=sQuery(id+"F2.wireOp",EDGE,"E3");var subQ11=sQuery(id+"F2.wireOp",EDGE,"E2");var subQ12=sQuery(id+"F2.wireOp",EDGE,"E1");var subQ13=sQuery(id+"F2.wireOp",EDGE,"E0");var subQ14=sQuery(id+"F2.wireOp",EDGE,"E21");var subQ15=sQuery(id+"F2.wireOp",EDGE,"E20");var subQ16=sQuery(id+"F2.wireOp",EDGE,"E18");var subQ17=sQuery(id+"F2.wireOp",EDGE,"E17");var subQ18=sQuery(id+"F2.wireOp",EDGE,"E16");var subQ19=sQuery(id+"F2.wireOp",EDGE,"E15");var subQ20=sQuery(id+"F2.wireOp",EDGE,"E13");var subQ21=sQuery(id+"F2.wireOp",EDGE,"E12");Q2=makeQuery(id+"F6.opShell","OFFSET_FACE",FACE,{"disambiguationData":[OSD([subQ13,subQ12,subQ11,subQ10,subQ9,subQ8,subQ7,subQ3,subQ2,subQ1,subQ6,subQ5,subQ21,subQ20,subQ0,subQ19,subQ18,subQ17,subQ16,subQ4,subQ15,subQ14]),TDD([makeQuery(id+"F5.boolean.opBoolean","MERGE",FACE,{"derivedFrom":[makeQuery(id+"F4.boolean.opBoolean","MERGE",FACE,{"derivedFrom":[makeQuery(id+"F3.opExtrude","CAP_FACE",FACE,{"disambiguationData":[OSD([subQ8,subQ5,subQ21,subQ20,subQ0,subQ19,subQ18,subQ17,subQ16,subQ4,subQ15,subQ14])],"isStart":false}),makeQuery(id+"F4.opExtrude","CAP_FACE",FACE,{"disambiguationData":[OSD([subQ13,subQ12,subQ11,subQ10,subQ9,subQ8,subQ7,subQ6,subQ5,subQ4])],"isStart":false})]}),makeQuery(id+"F5.opExtrude","CAP_FACE",FACE,{"disambiguationData":[OSD([subQ3,subQ2,subQ1,subQ0])],"isStart":false})]})]),OD(1.0)]});}
            extrude(context, id + "F11", {"entities" : qUnion([Q0, Q1, Q2]), "operationType" : NewBodyOperationType.ADD, "depth" : 3 * mm});
        }
    });
